# Revit family: Sink-Undermount-American_Standard-Pekoe-18SB.8171700.075
name_source: partatom
category: Plumbing Fixtures
revit_build: Autodesk Revit 2014 (Build: 20130308_1515(x64)
units: mm (PartAtom-declared; Revit-internal decimal feet)

## types (1)
- 18SB.8171700.075
    Assembly Code = D2010410
    Basin Shape = Square
    CW Connection = Yes
    CWFU = 3
    Cold Water Connection Diameter = 1/2"
    Cold Water Connection Radius = 1/4"
    Cold Water Connection Width = 4"
    Default Elevation = 34"
    Description = Pekoe Kitchen Sink
    Finish = Stainless Steel-American Standard-075-Satin
    HW Connection = Yes
    HWFU = 3
    Height = 8"
    Hot Water Connection Diameter = 1"
    Hot Water Connection Radius = 1/4"
    Hot Water Connection Width = 4"
    Installation Type = Undermount
    Length = 17"
    Manufacturer = American Standard
    Material = Stainless Steel-American Standard-075-Satin
    Model = 18SB.8171700.075
    Price = Prices may vary. Please consult Manufacturer Representative for most up-to-date price list.
    Product Documentation Link = https://www.americanstandard-us.com
    Product Page URL = https://www.americanstandard-us.com
    Revised Date = 01/04/2019
    URL = https://www.americanstandard-us.com
    Vent Connection = No
    WFU = 4
    Wall Distance = 4"
    Warranty Information = Limited Lifetime Warranty
    Waste Connection = Yes
    Waste Connection Diameter = 1 1/2"
    Waste Connection Radius = 3/4"
    Width = 17"

## geometry (parser evidence)
native form markers: Sweep x1
no freeform markers — native parametric forms only
